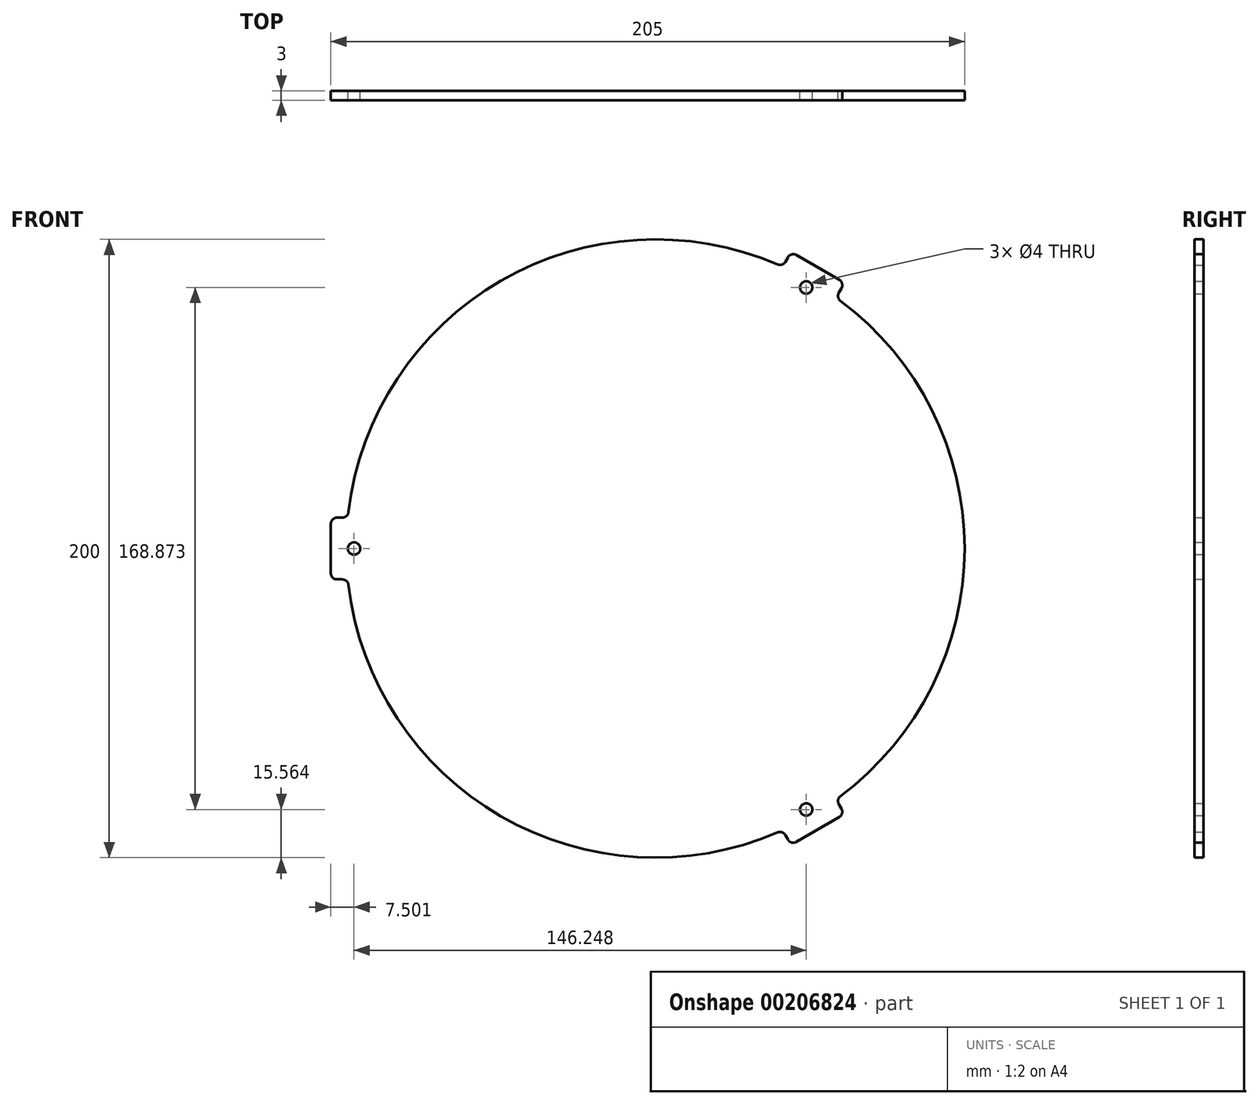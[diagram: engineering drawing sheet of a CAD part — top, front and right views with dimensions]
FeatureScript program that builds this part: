
annotation { "Feature Type Name" : "Feature", "Feature Type Description" : "" }
export const myFeature = defineFeature(function(context is Context, id is Id, definition is map)
    precondition{}
    {
        {
            var Q0;
            Q0=qCreatedBy(makeId("Front.planeOp"),FACE);
            var sketch = newSketch(context, id + "F0", { "sketchPlane" : qUnion([Q0])});
            skArc(sketch, "E0", {"start": v(-99.5, -10) * mm, "mid": v(-50, -86.6) * mm, "end": v(41.09, -91.17) * mm});
            skLineSegment(sketch, "E1", {"start": v(0, 0) * mm, "end": v(63.3, 109.65) * mm, "construction": true});
            skLineSegment(sketch, "E2", {"start": v(0, 0) * mm, "end": v(70.88, -122.77) * mm, "construction": true});
            skLineSegment(sketch, "E3", {"start": v(0, 0) * mm, "end": v(-175.52, 0) * mm, "construction": true});
            skCircle(sketch, "E4", {"center": v(0, 0) * mm, "radius": 105 * mm, "construction": true});
            skArc(sketch, "E5.trimOffspring", {"start": v(58.4, -81.17) * mm, "mid": v(100, 0) * mm, "end": v(58.4, 81.17) * mm});
            skArc(sketch, "E6.trimOffspring", {"start": v(41.09, 91.17) * mm, "mid": v(-50, 86.6) * mm, "end": v(-99.5, 10) * mm});
            skLineSegment(sketch, "E7", {"start": v(-105, 10) * mm, "end": v(-105, -10) * mm});
            skLineSegment(sketch, "E8", {"start": v(-105, 10) * mm, "end": v(-99.5, 10) * mm});
            skLineSegment(sketch, "E9.MirrorCS", {"start": v(-105, -10) * mm, "end": v(-99.5, -10) * mm});
            skLineSegment(sketch, "E10.1.0", {"start": v(43.84, -95.93) * mm, "end": v(41.09, -91.17) * mm});
            skLineSegment(sketch, "E10.1.1", {"start": v(43.84, -95.93) * mm, "end": v(61.16, -85.93) * mm});
            skLineSegment(sketch, "E10.1.2", {"start": v(61.16, -85.93) * mm, "end": v(58.4, -81.17) * mm});
            skLineSegment(sketch, "E10.2.0", {"start": v(61.16, 85.93) * mm, "end": v(58.4, 81.17) * mm});
            skLineSegment(sketch, "E10.2.1", {"start": v(61.16, 85.93) * mm, "end": v(43.84, 95.93) * mm});
            skLineSegment(sketch, "E10.2.2", {"start": v(43.84, 95.93) * mm, "end": v(41.09, 91.17) * mm});
            skCircle(sketch, "E11", {"center": v(-97.5, 0) * mm, "radius": 2 * mm});
            skCircle(sketch, "E12.1.0", {"center": v(48.75, -84.44) * mm, "radius": 2 * mm});
            skCircle(sketch, "E12.2.0", {"center": v(48.75, 84.44) * mm, "radius": 2 * mm});
            skCircle(sketch, "E13", {"center": v(0, 0) * mm, "radius": 97.5 * mm, "construction": true});
            skLineSegment(sketch, "E14", {"start": v(-99.5, 10) * mm, "end": v(-99.5, -10) * mm, "construction": true});
            skSolve(sketch);
        }
        {
            var Q0;
            Q0 = qSketchRegion(id + "F0", true);
            extrude(context, id + "F1", {"entities" : qUnion([Q0]), "depth" : 3 * mm});
        }
        {
            var Q0;
            Q0=makeQuery(id+"F1.opExtrude","SWEPT_EDGE",EDGE,{"disambiguationData":[OSD([sQuery(id+"F0.wireOp",EDGE,"E5.trimOffspring"),sQuery(id+"F0.wireOp",EDGE,"E10.2.0")])]});
            var Q1;
            Q1=makeQuery(id+"F1.opExtrude","SWEPT_EDGE",EDGE,{"disambiguationData":[OSD([sQuery(id+"F0.wireOp",EDGE,"E6.trimOffspring"),sQuery(id+"F0.wireOp",EDGE,"E10.2.2")])]});
            var Q2;
            Q2=makeQuery(id+"F1.opExtrude","SWEPT_EDGE",EDGE,{"disambiguationData":[OSD([sQuery(id+"F0.wireOp",EDGE,"E5.trimOffspring"),sQuery(id+"F0.wireOp",EDGE,"E10.1.2")])]});
            var Q3;
            Q3=makeQuery(id+"F1.opExtrude","SWEPT_EDGE",EDGE,{"disambiguationData":[OSD([sQuery(id+"F0.wireOp",EDGE,"E0"),sQuery(id+"F0.wireOp",EDGE,"E10.1.0")])]});
            var Q4;
            Q4=makeQuery(id+"F1.opExtrude","SWEPT_EDGE",EDGE,{"disambiguationData":[OSD([sQuery(id+"F0.wireOp",EDGE,"E0"),sQuery(id+"F0.wireOp",EDGE,"E9.MirrorCS")])]});
            var Q5;
            Q5=makeQuery(id+"F1.opExtrude","SWEPT_EDGE",EDGE,{"disambiguationData":[OSD([sQuery(id+"F0.wireOp",EDGE,"E6.trimOffspring"),sQuery(id+"F0.wireOp",EDGE,"E8")])]});
            fillet(context, id + "F2", {"entities" : qUnion([Q0, Q1, Q2, Q3, Q4, Q5]), "radius" : 2 * mm, "tangentPropagation" : true, "allowEdgeOverflow" : false});
        }
        {
            var Q0;
            Q0=makeQuery(id+"F1.opExtrude","SWEPT_EDGE",EDGE,{"disambiguationData":[OSD([sQuery(id+"F0.wireOp",EDGE,"E10.2.0"),sQuery(id+"F0.wireOp",EDGE,"E10.2.1")])]});
            var Q1;
            Q1=makeQuery(id+"F1.opExtrude","SWEPT_EDGE",EDGE,{"disambiguationData":[OSD([sQuery(id+"F0.wireOp",EDGE,"E10.2.1"),sQuery(id+"F0.wireOp",EDGE,"E10.2.2")])]});
            var Q2;
            Q2=makeQuery(id+"F1.opExtrude","SWEPT_EDGE",EDGE,{"disambiguationData":[OSD([sQuery(id+"F0.wireOp",EDGE,"E7"),sQuery(id+"F0.wireOp",EDGE,"E8")])]});
            var Q3;
            Q3=makeQuery(id+"F1.opExtrude","SWEPT_EDGE",EDGE,{"disambiguationData":[OSD([sQuery(id+"F0.wireOp",EDGE,"E7"),sQuery(id+"F0.wireOp",EDGE,"E9.MirrorCS")])]});
            var Q4;
            Q4=makeQuery(id+"F1.opExtrude","SWEPT_EDGE",EDGE,{"disambiguationData":[OSD([sQuery(id+"F0.wireOp",EDGE,"E10.1.0"),sQuery(id+"F0.wireOp",EDGE,"E10.1.1")])]});
            var Q5;
            Q5=makeQuery(id+"F1.opExtrude","SWEPT_EDGE",EDGE,{"disambiguationData":[OSD([sQuery(id+"F0.wireOp",EDGE,"E10.1.1"),sQuery(id+"F0.wireOp",EDGE,"E10.1.2")])]});
            fillet(context, id + "F3", {"entities" : qUnion([Q0, Q1, Q2, Q3, Q4, Q5]), "radius" : 2 * mm, "tangentPropagation" : true, "allowEdgeOverflow" : false});
        }
    });
